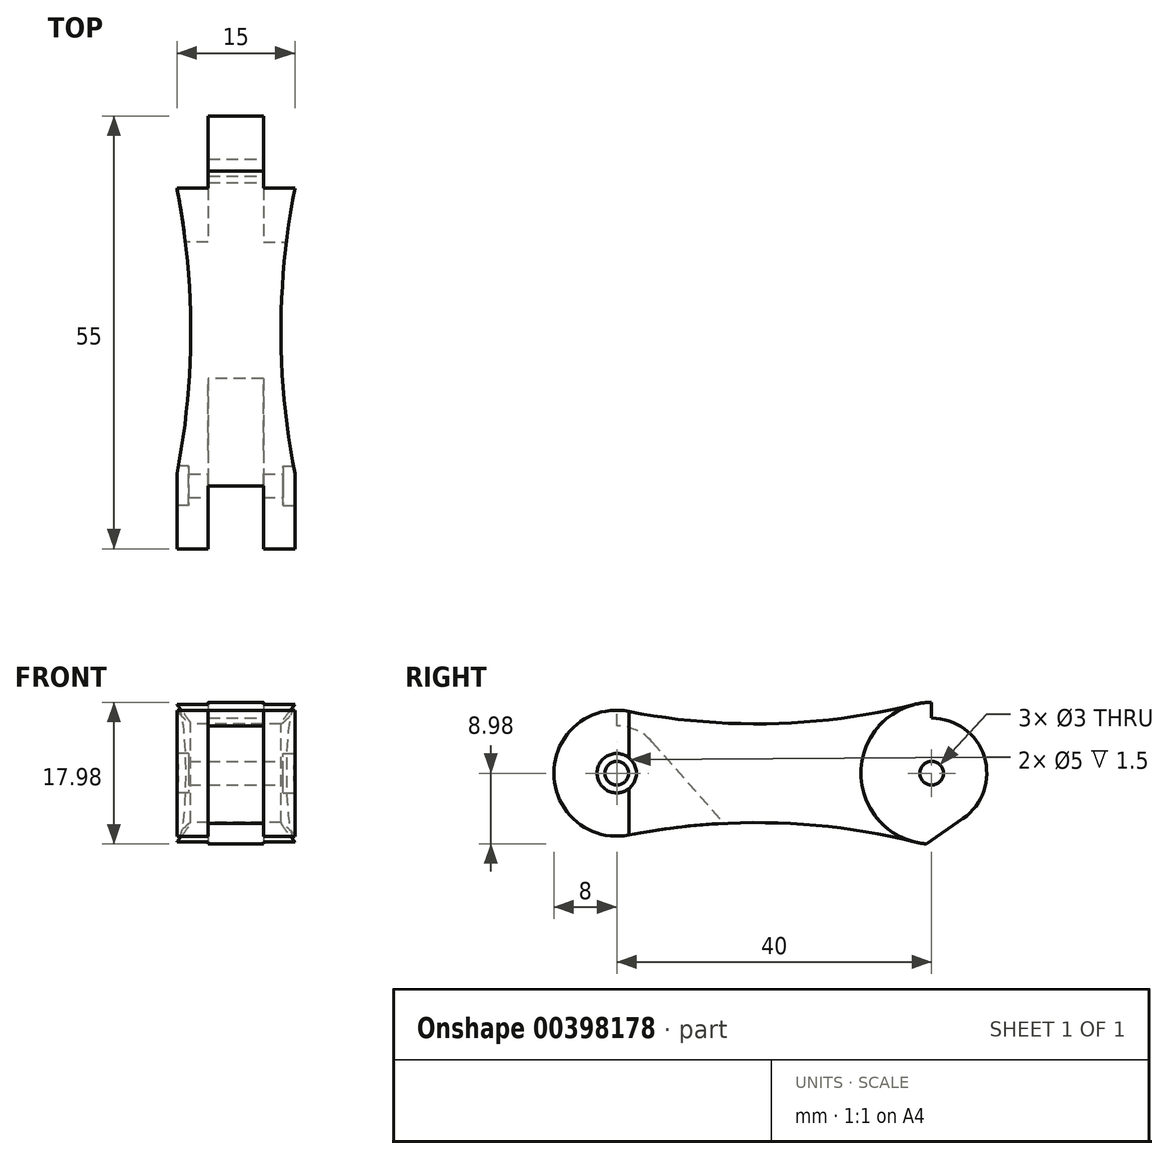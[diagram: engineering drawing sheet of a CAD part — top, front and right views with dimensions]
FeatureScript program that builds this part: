
annotation { "Feature Type Name" : "Feature", "Feature Type Description" : "" }
export const myFeature = defineFeature(function(context is Context, id is Id, definition is map)
    precondition{}
    {
        {
            var Q0;
            Q0=qCreatedBy(makeId("Right.planeOp"),FACE);
            var sketch = newSketch(context, id + "F0", { "sketchPlane" : qUnion([Q0])});
            skArc(sketch, "E0", {"start": v(1.54, 7.85) * mm, "mid": v(-8, 0) * mm, "end": v(1.54, -7.85) * mm});
            skLineSegment(sketch, "E1", {"start": v(-29.92, 0) * mm, "end": v(87.26, 0) * mm, "construction": true});
            skArc(sketch, "E2", {"start": v(37.83, -8.74) * mm, "mid": v(49, 0) * mm, "end": v(37.83, 8.74) * mm});
            skArc(sketch, "E3", {"start": v(1.54, 7.85) * mm, "mid": v(19.74, 6.3) * mm, "end": v(37.83, 8.74) * mm});
            skArc(sketch, "E4", {"start": v(37.83, -8.74) * mm, "mid": v(19.74, -6.3) * mm, "end": v(1.54, -7.85) * mm});
            skSolve(sketch);
        }
        {
            var Q0;
            Q0=qSketchRegion(id+"F0",true);
            extrude(context, id + "F1", {"entities" : qUnion([Q0]), "depth" : 4 * mm});
        }
        {
            var Q0;
            Q0=makeQuery(id+"F1.opExtrude","CAP_FACE",FACE,{"disambiguationData":[OSD([sQuery(id+"F0.wireOp",EDGE,"E0"),sQuery(id+"F0.wireOp",EDGE,"E2"),sQuery(id+"F0.wireOp",EDGE,"E3"),sQuery(id+"F0.wireOp",EDGE,"E4")])],"isStart":false});
            var sketch = newSketch(context, id + "F2", { "sketchPlane" : qUnion([Q0])});
            skArc(sketch, "E5.0", {"start": v(37.83, -8.74) * mm, "mid": v(49, 0) * mm, "end": v(37.83, 8.74) * mm});
            skLineSegment(sketch, "E6", {"start": v(0, 0) * mm, "end": v(34.9, 0) * mm, "construction": true});
            skArc(sketch, "E7.0", {"start": v(1.54, 7.85) * mm, "mid": v(19.74, 6.3) * mm, "end": v(37.83, 8.74) * mm});
            skArc(sketch, "E8.0", {"start": v(37.83, -8.74) * mm, "mid": v(25.82, -6.67) * mm, "end": v(13.62, -6.38) * mm});
            skArc(sketch, "E9.0", {"start": v(1.54, 7.85) * mm, "mid": v(0.78, 7.96) * mm, "end": v(0, 8) * mm});
            skArc(sketch, "E10", {"start": v(4.5, 3.97) * mm, "mid": v(2.47, 5.47) * mm, "end": v(0, 6) * mm});
            skLineSegment(sketch, "E11", {"start": v(0, 6) * mm, "end": v(0, 8) * mm});
            skLineSegment(sketch, "E12", {"start": v(4.5, 3.97) * mm, "end": v(13.62, -6.38) * mm});
            skPoint(sketch, "E13.orphan", {"position": v(1.54, -7.85) * mm});
            skSolve(sketch);
        }
        {
            var Q0;
            Q0=qSketchRegion(id+"F2",true);
            extrude(context, id + "F3", {"entities" : qUnion([Q0]), "operationType" : NewBodyOperationType.ADD, "depth" : 7 * mm});
        }
        {
            var Q0;
            Q0=makeQuery(id+"F3.opExtrude","CAP_FACE",FACE,{"disambiguationData":[OSD([sQuery(id+"F2.wireOp",EDGE,"3bf56276-6e63-42ee-98d8-77259c1c36c8.0"),sQuery(id+"F2.wireOp",EDGE,"bc38228c-ca1f-41e0-8e1d-5deb207440e8.0"),sQuery(id+"F2.wireOp",EDGE,"a1095cbb-552a-4b33-82fb-9fb0068e6b7f.0"),sQuery(id+"F2.wireOp",EDGE,"E5.0"),sQuery(id+"F2.wireOp",EDGE,"kkhRfJHV-auDH-NZtS-KPEK-8B2iLmtzf0xF"),sQuery(id+"F2.wireOp",EDGE,"MWx028tx-hoiO-j3L1-AWWv-dpKiWbue3HpV"),sQuery(id+"F2.wireOp",EDGE,"JRJ70NO1-7vJe-Li3z-EIXT-plhISmGAnEbH")])],"isStart":false});
            var sketch = newSketch(context, id + "F4", { "sketchPlane" : qUnion([Q0])});
            skArc(sketch, "E14.0", {"start": v(1.54, 7.85) * mm, "mid": v(19.74, 6.3) * mm, "end": v(37.83, 8.74) * mm});
            skArc(sketch, "E15.0", {"start": v(0, 8) * mm, "mid": v(-7.96, -0.78) * mm, "end": v(1.54, -7.85) * mm});
            skArc(sketch, "E16.0", {"start": v(1.54, 7.85) * mm, "mid": v(0.78, 7.96) * mm, "end": v(0, 8) * mm});
            skArc(sketch, "E17.0", {"start": v(13.62, -6.38) * mm, "mid": v(7.56, -6.9) * mm, "end": v(1.54, -7.85) * mm});
            skArc(sketch, "E18.0", {"start": v(37.83, -8.74) * mm, "mid": v(25.82, -6.67) * mm, "end": v(13.62, -6.38) * mm});
            skArc(sketch, "E19.0", {"start": v(37.83, -8.74) * mm, "mid": v(49, 0) * mm, "end": v(37.83, 8.74) * mm});
            skSolve(sketch);
        }
        {
            var Q0;
            Q0=qSketchRegion(id+"F4",true);
            extrude(context, id + "F5", {"entities" : qUnion([Q0]), "operationType" : NewBodyOperationType.ADD, "depth" : 4 * mm});
        }
        {
            var Q0;
            {var subQ0=sQuery(id+"F4.wireOp",EDGE,"E19.0");Q0=makeQuery(id+"F13.boolean.opBoolean","SPLIT",FACE,{"disambiguationData":[TD([makeQuery(id+"F1.opExtrude","SWEPT_FACE",FACE,{"disambiguationData":[OSD([sQuery(id+"F0.wireOp",EDGE,"E2")])]})])],"derivedFrom":makeQuery(id+"F5.opExtrude","CAP_FACE",FACE,{"disambiguationData":[OSD([sQuery(id+"F4.wireOp",EDGE,"E14.0"),sQuery(id+"F4.wireOp",EDGE,"E15.0"),sQuery(id+"F4.wireOp",EDGE,"E16.0"),sQuery(id+"F4.wireOp",EDGE,"E17.0"),sQuery(id+"F4.wireOp",EDGE,"E18.0"),subQ0])],"isStart":false})});}
            var sketch = newSketch(context, id + "F6", { "sketchPlane" : qUnion([Q0])});
            skCircle(sketch, "E20", {"center": v(40, 0) * mm, "radius": 9 * mm});
            skSolve(sketch);
        }
        {
            var Q0;
            Q0=qSketchRegion(id+"F6",true);
            extrude(context, id + "F7", {"entities" : qUnion([Q0]), "operationType" : NewBodyOperationType.REMOVE, "oppositeDirection" : true, "depth" : 4 * mm});
        }
        {
            var Q0;
            Q0=makeQuery(id+"F1.opExtrude","CAP_FACE",FACE,{"disambiguationData":[OSD([sQuery(id+"F0.wireOp",EDGE,"E0"),sQuery(id+"F0.wireOp",EDGE,"E2"),sQuery(id+"F0.wireOp",EDGE,"E3"),sQuery(id+"F0.wireOp",EDGE,"E4")])],"isStart":true});
            var sketch = newSketch(context, id + "F8", { "sketchPlane" : qUnion([Q0])});
            skCircle(sketch, "E21", {"center": v(-40, 0) * mm, "radius": 9 * mm});
            skSolve(sketch);
        }
        {
            var Q0;
            Q0=qSketchRegion(id+"F8",true);
            extrude(context, id + "F9", {"entities" : qUnion([Q0]), "operationType" : NewBodyOperationType.REMOVE, "oppositeDirection" : true, "depth" : 4 * mm});
        }
        {
            var Q0;
            Q0=makeQuery(id+"F1.opExtrude","CAP_FACE",FACE,{"disambiguationData":[OSD([sQuery(id+"F0.wireOp",EDGE,"E0"),sQuery(id+"F0.wireOp",EDGE,"E2"),sQuery(id+"F0.wireOp",EDGE,"E3"),sQuery(id+"F0.wireOp",EDGE,"E4")])],"isStart":true});
            var sketch = newSketch(context, id + "F10", { "sketchPlane" : qUnion([Q0])});
            skCircle(sketch, "E22", {"center": v(0, 0) * mm, "radius": 2.5 * mm});
            skSolve(sketch);
        }
        {
            var Q0;
            Q0=qSketchRegion(id+"F10",true);
            extrude(context, id + "F11", {"entities" : qUnion([Q0]), "operationType" : NewBodyOperationType.REMOVE, "oppositeDirection" : true, "depth" : 1.5 * mm});
        }
        {
            var Q0;
            Q0=qCreatedBy(makeId("Top.planeOp"),FACE);
            var sketch = newSketch(context, id + "F12", { "sketchPlane" : qUnion([Q0])});
            skCircle(sketch, "E23", {"center": v(-92, 19.69) * mm, "radius": 93.77 * mm});
            skCircle(sketch, "E24", {"center": v(107, 19.69) * mm, "radius": 93.77 * mm});
            skSolve(sketch);
        }
        {
            var Q0;
            Q0=qSketchRegion(id+"F12",true);
            extrude(context, id + "F13", {"entities" : qUnion([Q0]), "operationType" : NewBodyOperationType.REMOVE, "endBound" : BoundingType.SYMMETRIC, "oppositeDirection" : true, "depth" : 25 * mm});
        }
        {
            var Q0;
            Q0=makeQuery(id+"F7.boolean.opBoolean","COPY",FACE,{"derivedFrom":makeQuery(id+"F7.opExtrude","CAP_FACE",FACE,{"disambiguationData":[OSD([sQuery(id+"F6.wireOp",EDGE,"E20")])],"isStart":false})});
            var sketch = newSketch(context, id + "F14", { "sketchPlane" : qUnion([Q0])});
            skCircle(sketch, "E25", {"center": v(40, 0) * mm, "radius": 1.5 * mm});
            skSolve(sketch);
        }
        {
            var Q0;
            Q0=qSketchRegion(id+"F14",true);
            extrude(context, id + "F15", {"entities" : qUnion([Q0]), "operationType" : NewBodyOperationType.REMOVE, "endBound" : BoundingType.THROUGH_ALL, "oppositeDirection" : true, "depth" : 25 * mm});
        }
        {
            var Q0;
            Q0=makeQuery(id+"F5.opExtrude","CAP_FACE",FACE,{"disambiguationData":[OSD([sQuery(id+"F4.wireOp",EDGE,"E14.0"),sQuery(id+"F4.wireOp",EDGE,"E15.0"),sQuery(id+"F4.wireOp",EDGE,"E16.0"),sQuery(id+"F4.wireOp",EDGE,"E17.0"),sQuery(id+"F4.wireOp",EDGE,"E18.0"),sQuery(id+"F4.wireOp",EDGE,"E19.0")])],"isStart":false});
            var sketch = newSketch(context, id + "F16", { "sketchPlane" : qUnion([Q0])});
            skCircle(sketch, "E26", {"center": v(0, 0) * mm, "radius": 1.5 * mm});
            skSolve(sketch);
        }
        {
            var Q0;
            Q0=qSketchRegion(id+"F16",true);
            extrude(context, id + "F17", {"entities" : qUnion([Q0]), "operationType" : NewBodyOperationType.REMOVE, "endBound" : BoundingType.THROUGH_ALL, "oppositeDirection" : true, "depth" : 25 * mm});
        }
        {
            var Q0;
            Q0=makeQuery(id+"F5.opExtrude","CAP_FACE",FACE,{"disambiguationData":[OSD([sQuery(id+"F4.wireOp",EDGE,"E14.0"),sQuery(id+"F4.wireOp",EDGE,"E15.0"),sQuery(id+"F4.wireOp",EDGE,"E16.0"),sQuery(id+"F4.wireOp",EDGE,"E17.0"),sQuery(id+"F4.wireOp",EDGE,"E18.0"),sQuery(id+"F4.wireOp",EDGE,"E19.0")])],"isStart":false});
            var sketch = newSketch(context, id + "F18", { "sketchPlane" : qUnion([Q0])});
            skCircle(sketch, "E27", {"center": v(0, 0) * mm, "radius": 2.5 * mm});
            skSolve(sketch);
        }
        {
            var Q0;
            Q0=qSketchRegion(id+"F18",true);
            extrude(context, id + "F19", {"entities" : qUnion([Q0]), "operationType" : NewBodyOperationType.REMOVE, "oppositeDirection" : true, "depth" : 1.5 * mm});
        }
        {
            var Q0;
            Q0=makeQuery(id+"F7.boolean.opBoolean","COPY",FACE,{"derivedFrom":makeQuery(id+"F7.opExtrude","CAP_FACE",FACE,{"disambiguationData":[OSD([sQuery(id+"F6.wireOp",EDGE,"E20")])],"isStart":false})});
            var sketch = newSketch(context, id + "F20", { "sketchPlane" : qUnion([Q0])});
            skArc(sketch, "E28", {"start": v(44, -5.74) * mm, "mid": v(46.68, 2.1) * mm, "end": v(40, 7) * mm});
            skArc(sketch, "E29.0", {"start": v(39.36, -8.98) * mm, "mid": v(49, -0.32) * mm, "end": v(40, 9) * mm});
            skLineSegment(sketch, "E30", {"start": v(40, 7) * mm, "end": v(40, 9) * mm});
            skLineSegment(sketch, "E31", {"start": v(44, -5.74) * mm, "end": v(39.36, -8.98) * mm});
            skPoint(sketch, "E32.orphan", {"position": v(37.83, -8.74) * mm});
            skPoint(sketch, "E33.orphan", {"position": v(37.83, 8.74) * mm});
            skSolve(sketch);
        }
        {
            var Q0;
            Q0=qSketchRegion(id+"F20",true);
            extrude(context, id + "F21", {"entities" : qUnion([Q0]), "operationType" : NewBodyOperationType.REMOVE, "endBound" : BoundingType.THROUGH_ALL, "oppositeDirection" : true, "depth" : 25 * mm});
        }
    });
